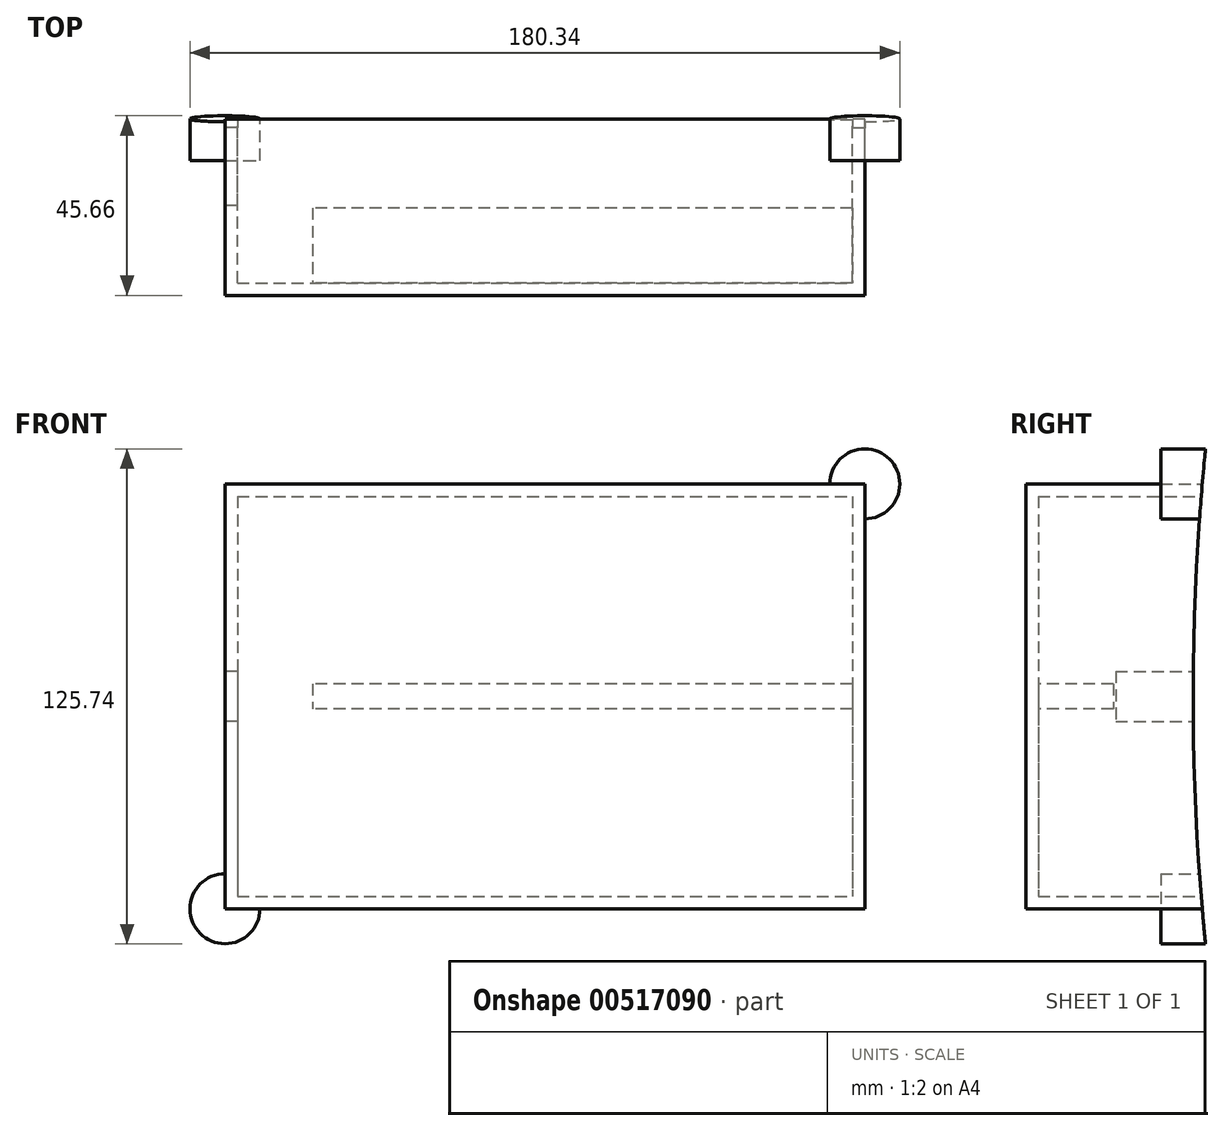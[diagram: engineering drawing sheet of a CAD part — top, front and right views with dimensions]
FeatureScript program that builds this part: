
annotation { "Feature Type Name" : "Feature", "Feature Type Description" : "" }
export const myFeature = defineFeature(function(context is Context, id is Id, definition is map)
    precondition{}
    {
        {
            var Q0;
            Q0=qCreatedBy(makeId("Front.planeOp"),FACE);
            var sketch = newSketch(context, id + "F0", { "sketchPlane" : qUnion([Q0])});
            skLineSegment(sketch, "E0.bottom", {"start": v(-81.28, 53.97) * mm, "end": v(81.28, 53.97) * mm});
            skLineSegment(sketch, "E0.top", {"start": v(-81.28, -53.98) * mm, "end": v(81.28, -53.97) * mm});
            skLineSegment(sketch, "E0.left", {"start": v(-81.28, 53.97) * mm, "end": v(-81.28, -53.98) * mm});
            skLineSegment(sketch, "E0.right", {"start": v(81.28, 53.97) * mm, "end": v(81.28, -53.97) * mm});
            skPoint(sketch, "E0.middle", {"position": v(0, 0) * mm});
            skArc(sketch, "E1", {"start": v(-81.28, 45.08) * mm, "mid": v(-87.57, 60.26) * mm, "end": v(-72.4, 53.98) * mm});
            skLineSegment(sketch, "E2", {"start": v(-83.97, 56.67) * mm, "end": v(-81.28, 53.97) * mm});
            skArc(sketch, "E3.MirrorCS", {"start": v(81.28, 45.08) * mm, "mid": v(87.57, 60.26) * mm, "end": v(72.4, 53.98) * mm});
            skArc(sketch, "E4.MirrorCS", {"start": v(-81.28, -45.08) * mm, "mid": v(-87.57, -60.26) * mm, "end": v(-72.4, -53.98) * mm});
            skArc(sketch, "E5.MirrorCS", {"start": v(81.28, -45.08) * mm, "mid": v(87.57, -60.26) * mm, "end": v(72.4, -53.98) * mm});
            skSolve(sketch);
        }
        {
            var Q0;
            {var subQ0=sQuery(id+"F0.wireOp",EDGE,"E0.left");Q0=makeQuery(id+"F0.imprint","IMPRINT",FACE,{"disambiguationData":[TD([[makeQuery(id+"F0.imprint","IMPRINT",EDGE,{"derivedFrom":subQ0}),1.0]])]});}
            extrude(context, id + "F1", {"entities" : qUnion([Q0]), "depth" : 47 * mm, "offsetDistance" : 25.4 * mm});
        }
        {
            var Q0;
            Q0=makeQuery(id+"F1.opExtrude","CAP_FACE",FACE,{"disambiguationData":[OSD([sQuery(id+"F0.wireOp",EDGE,"E0.bottom"),sQuery(id+"F0.wireOp",EDGE,"E0.top"),sQuery(id+"F0.wireOp",EDGE,"E0.left"),sQuery(id+"F0.wireOp",EDGE,"E0.right")])],"isStart":true});
            shell(context, id + "F2", {"entities" : qUnion([Q0]), "thickness" : 3.17 * mm});
        }
        {
            var Q0;
            Q0=makeQuery(id+"F1.opExtrude","SWEPT_FACE",FACE,{"disambiguationData":[OSD([sQuery(id+"F0.wireOp",EDGE,"E0.left")])]});
            cPlane(context, id + "F3", {"entities" : qUnion([Q0]), "cplaneType" : CPlaneType.OFFSET, "offset" : 25.4 * mm, "width" : 152.4 * mm, "height" : 152.4 * mm});
        }
        {
            var Q0;
            Q0=makeQuery(id+"F1.opExtrude","SWEPT_FACE",FACE,{"disambiguationData":[OSD([sQuery(id+"F0.wireOp",EDGE,"E0.left")])]});
            var sketch = newSketch(context, id + "F4", { "sketchPlane" : qUnion([Q0])});
            skLineSegment(sketch, "E6", {"start": v(13.97, 0) * mm, "end": v(0, 0) * mm});
            skLineSegment(sketch, "E7", {"start": v(13.97, 0) * mm, "end": v(47, 0) * mm});
            skLineSegment(sketch, "E8.bottom", {"start": v(24.13, 6.35) * mm, "end": v(3.8, 6.35) * mm});
            skLineSegment(sketch, "E8.top", {"start": v(24.13, -6.35) * mm, "end": v(3.8, -6.35) * mm});
            skLineSegment(sketch, "E8.left", {"start": v(24.13, 6.35) * mm, "end": v(24.13, -6.35) * mm});
            skLineSegment(sketch, "E8.right", {"start": v(3.8, 6.35) * mm, "end": v(3.8, -6.35) * mm});
            skPoint(sketch, "E8.middle", {"position": v(13.97, 0) * mm});
            skSolve(sketch);
        }
        {
            var Q0;
            {var subQ3=sQuery(id+"F0.wireOp",EDGE,"E1");Q0=makeQuery(id+"F0.imprint","IMPRINT",FACE,{"disambiguationData":[TD([[makeQuery(id+"F0.imprint","IMPRINT",EDGE,{"derivedFrom":subQ3}),-1.0]])]});}
            var Q1;
            {var subQ3=sQuery(id+"F0.wireOp",EDGE,"E4.MirrorCS");Q1=makeQuery(id+"F0.imprint","IMPRINT",FACE,{"disambiguationData":[TD([[makeQuery(id+"F0.imprint","IMPRINT",EDGE,{"derivedFrom":subQ3}),1.0]])]});}
            var Q2;
            {var subQ3=sQuery(id+"F0.wireOp",EDGE,"E3.MirrorCS");Q2=makeQuery(id+"F0.imprint","IMPRINT",FACE,{"disambiguationData":[TD([[makeQuery(id+"F0.imprint","IMPRINT",EDGE,{"derivedFrom":subQ3}),1.0]])]});}
            var Q3;
            Q3=makeQuery(id+"F0.imprint","IMPRINT",FACE,{"disambiguationData":[TD([[makeQuery(id+"F0.imprint","IMPRINT",EDGE,{"derivedFrom":sQuery(id+"F0.wireOp",EDGE,"924e01de-4123-44ed-afe8-1053d54f82ae0.MirrorC")}),-1.0]])]});
            var Q4;
            {var subQ3=sQuery(id+"F0.wireOp",EDGE,"E5.MirrorCS");Q4=makeQuery(id+"F0.imprint","IMPRINT",FACE,{"disambiguationData":[TD([[makeQuery(id+"F0.imprint","IMPRINT",EDGE,{"derivedFrom":subQ3}),-1.0]])]});}
            extrude(context, id + "F5", {"entities" : qUnion([Q0, Q1, Q2, Q3, Q4]), "operationType" : NewBodyOperationType.ADD, "depth" : 12.7 * mm, "offsetDistance" : 25.4 * mm});
        }
        {
            var Q0;
            Q0=qCreatedBy(id+"F3.planeOp",FACE);
            var sketch = newSketch(context, id + "F6", { "sketchPlane" : qUnion([Q0])});
            skLineSegment(sketch, "E9", {"start": v(0, 0) * mm, "end": v(-630.56, 0) * mm});
            skCircle(sketch, "E10", {"center": v(-630.56, 0) * mm, "radius": 635 * mm});
            skSolve(sketch);
        }
        {
            var Q0;
            Q0=qSketchRegion(id+"F6",true);
            extrude(context, id + "F7", {"entities" : qUnion([Q0]), "operationType" : NewBodyOperationType.REMOVE, "oppositeDirection" : true, "depth" : 279.4 * mm});
        }
        {
            var Q0;
            Q0 = qSketchRegion(id + "F4", true);
            extrude(context, id + "F8", {"entities" : qUnion([Q0]), "operationType" : NewBodyOperationType.REMOVE, "oppositeDirection" : true, "depth" : 3.17 * mm, "offsetDistance" : 25.4 * mm});
        }
        {
            var Q0;
            Q0=makeQuery(id+"F2.opShell","OFFSET_FACE",FACE,{"disambiguationData":[OSD([sQuery(id+"F0.wireOp",EDGE,"E0.bottom"),sQuery(id+"F0.wireOp",EDGE,"E0.top"),sQuery(id+"F0.wireOp",EDGE,"E0.left"),sQuery(id+"F0.wireOp",EDGE,"E0.right")])]});
            var sketch = newSketch(context, id + "F9", { "sketchPlane" : qUnion([Q0])});
            skLineSegment(sketch, "E11", {"start": v(78.1, 0) * mm, "end": v(-78.1, 0) * mm});
            skLineSegment(sketch, "E12.bottom", {"start": v(-78.1, 3.18) * mm, "end": v(78.1, 3.17) * mm});
            skLineSegment(sketch, "E12.top", {"start": v(-78.1, -3.17) * mm, "end": v(78.1, -3.18) * mm});
            skLineSegment(sketch, "E12.left", {"start": v(-78.1, 3.18) * mm, "end": v(-78.1, -3.17) * mm});
            skLineSegment(sketch, "E12.right", {"start": v(78.1, 3.18) * mm, "end": v(78.1, -3.17) * mm});
            skPoint(sketch, "E12.middle", {"position": v(0, 0) * mm});
            skLineSegment(sketch, "E13.bottom", {"start": v(-78.1, 3.18) * mm, "end": v(59.06, 3.18) * mm});
            skLineSegment(sketch, "E13.top", {"start": v(-78.1, -3.18) * mm, "end": v(59.06, -3.18) * mm});
            skLineSegment(sketch, "E13.right", {"start": v(59.06, 3.18) * mm, "end": v(59.06, -3.17) * mm});
            skSolve(sketch);
        }
        {
            var Q0;
            {var subQ0=sQuery(id+"F9.wireOp",EDGE,"E13.right");var subQ1=sQuery(id+"F9.wireOp",EDGE,"E11");var subQ2=makeQuery(id+"F9.imprint","INTERSECT",VERTEX,{"derivedFrom":[subQ1,subQ0]});Q0=makeQuery(id+"F9.imprint","IMPRINT",FACE,{"disambiguationData":[TD([[makeQuery(id+"F9.imprint","IMPRINT",EDGE,{"disambiguationData":[TD([[subQ2,-1.0]])],"derivedFrom":subQ1}),1.0]])]});}
            var Q1;
            {var subQ0=sQuery(id+"F9.wireOp",EDGE,"E13.right");var subQ1=sQuery(id+"F9.wireOp",EDGE,"E11");var subQ2=makeQuery(id+"F9.imprint","INTERSECT",VERTEX,{"derivedFrom":[subQ1,subQ0]});Q1=makeQuery(id+"F9.imprint","IMPRINT",FACE,{"disambiguationData":[TD([[makeQuery(id+"F9.imprint","IMPRINT",EDGE,{"disambiguationData":[TD([[subQ2,-1.0]])],"derivedFrom":subQ1}),-1.0]])]});}
            extrude(context, id + "F10", {"entities" : qUnion([Q0, Q1]), "operationType" : NewBodyOperationType.ADD, "depth" : 19.05 * mm, "offsetDistance" : 25.4 * mm});
        }
    });
